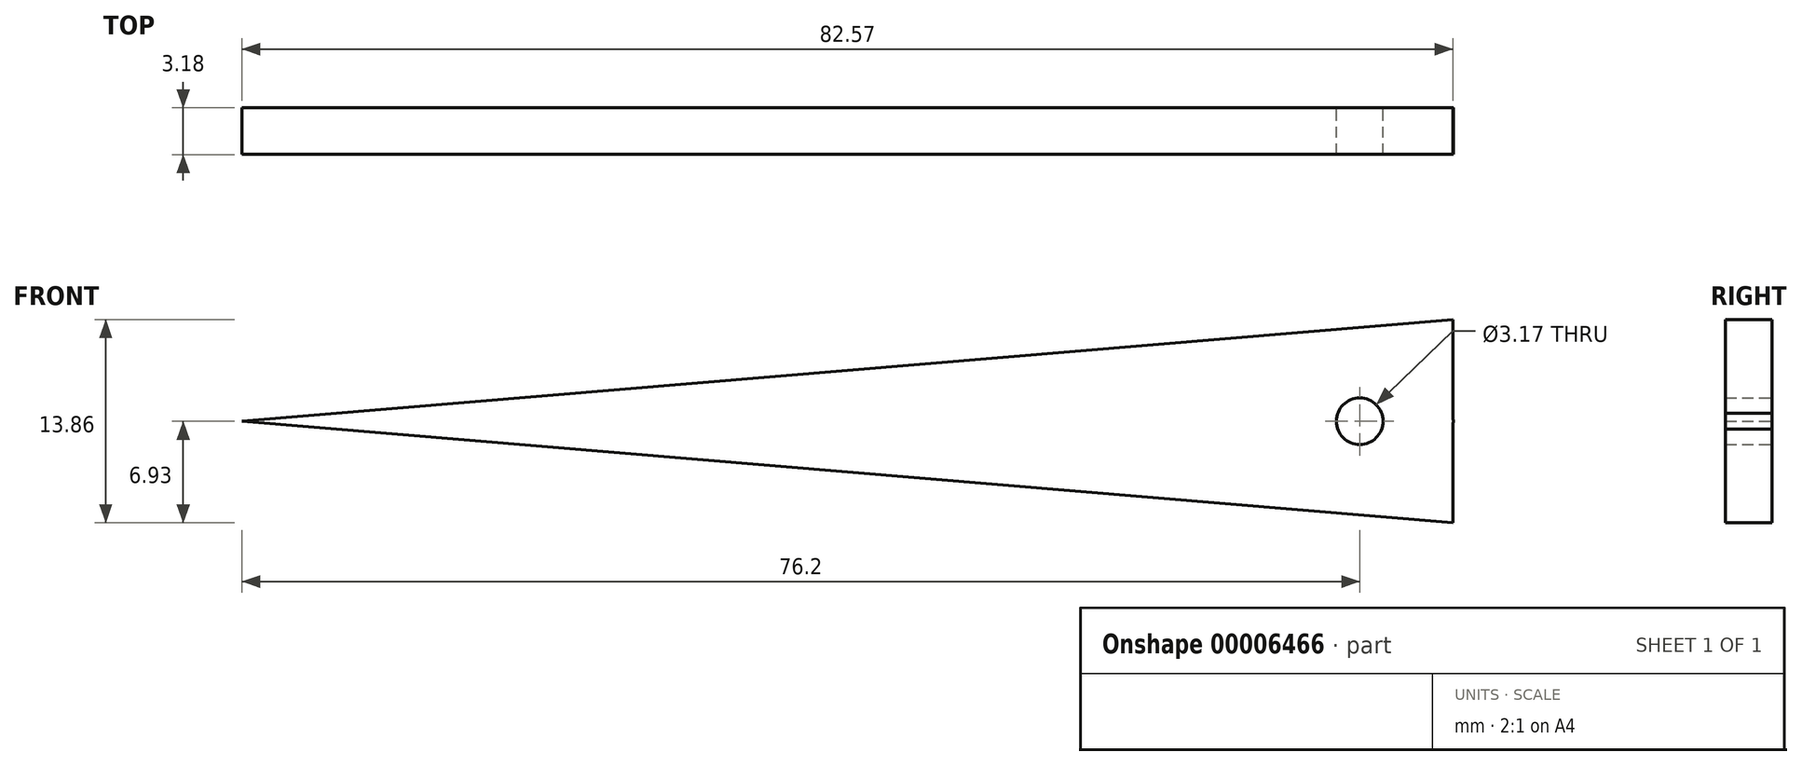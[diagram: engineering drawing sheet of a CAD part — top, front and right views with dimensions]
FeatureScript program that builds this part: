
annotation { "Feature Type Name" : "Feature", "Feature Type Description" : "" }
export const myFeature = defineFeature(function(context is Context, id is Id, definition is map)
    precondition{}
    {
        {
            var Q0;
            Q0=qCreatedBy(makeId("Front.planeOp"),FACE);
            var sketch = newSketch(context, id + "F0", { "sketchPlane" : qUnion([Q0])});
            skLineSegment(sketch, "E0", {"start": v(0, 0) * mm, "end": v(75.67, 6.35) * mm});
            skLineSegment(sketch, "E1", {"start": v(0, 0) * mm, "end": v(75.67, -6.35) * mm});
            skArc(sketch, "E2", {"start": v(75.67, -6.35) * mm, "mid": v(82.57, 0) * mm, "end": v(75.67, 6.35) * mm});
            skCircle(sketch, "E3", {"center": v(76.2, 0) * mm, "radius": 1.59 * mm});
            skLineSegment(sketch, "E4", {"start": v(82.55, 6.93) * mm, "end": v(82.55, -6.93) * mm});
            skLineSegment(sketch, "E5", {"start": v(82.55, -6.93) * mm, "end": v(75.67, -6.35) * mm});
            skLineSegment(sketch, "E6", {"start": v(75.67, 6.35) * mm, "end": v(82.55, 6.93) * mm});
            skSolve(sketch);
        }
        {
            var Q0;
            Q0 = qSketchRegion(id + "F0", true);
            extrude(context, id + "F1", {"entities" : qUnion([Q0]), "depth" : 3.17 * mm});
        }
    });
